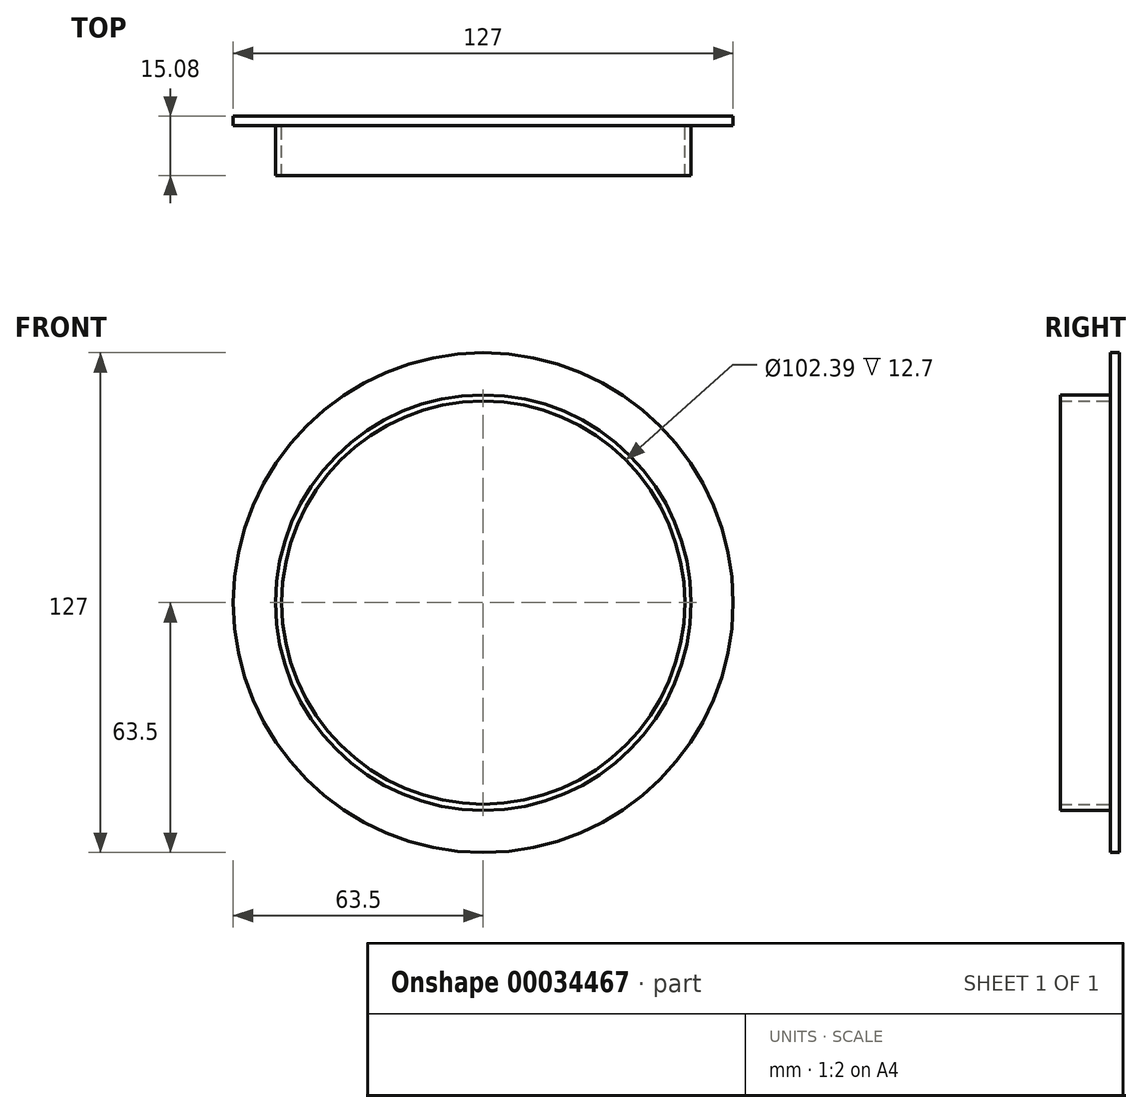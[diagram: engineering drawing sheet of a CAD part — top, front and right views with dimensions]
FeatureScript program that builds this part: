
annotation { "Feature Type Name" : "Feature", "Feature Type Description" : "" }
export const myFeature = defineFeature(function(context is Context, id is Id, definition is map)
    precondition{}
    {
        {
            var Q0;
            Q0=qCreatedBy(makeId("Front.planeOp"),FACE);
            var sketch = newSketch(context, id + "F0", { "sketchPlane" : qUnion([Q0])});
            skCircle(sketch, "E0", {"center": v(0, 0) * mm, "radius": 52.78 * mm});
            skCircle(sketch, "E1.0", {"center": v(0, 0) * mm, "radius": 51.2 * mm});
            skSolve(sketch);
        }
        {
            var Q0;
            Q0=makeQuery(id+"F0.imprint","IMPRINT",FACE,{"disambiguationData":[TD([[makeQuery(id+"F0.imprint","IMPRINT",EDGE,{"derivedFrom":sQuery(id+"F0.wireOp",EDGE,"E0")}),1.0]])]});
            extrude(context, id + "F1", {"entities" : qUnion([Q0]), "depth" : 12.7 * mm, "offsetDistance" : 25.4 * mm});
        }
        {
            var Q0;
            Q0=qCreatedBy(makeId("Front.planeOp"),FACE);
            var sketch = newSketch(context, id + "F2", { "sketchPlane" : qUnion([Q0])});
            skCircle(sketch, "E2", {"center": v(0, 0) * mm, "radius": 63.5 * mm});
            skSolve(sketch);
        }
        {
            var Q0;
            Q0 = qSketchRegion(id + "F2", true);
            extrude(context, id + "F3", {"entities" : qUnion([Q0]), "operationType" : NewBodyOperationType.ADD, "oppositeDirection" : true, "depth" : 2.38 * mm, "offsetDistance" : 25.4 * mm});
        }
    });
